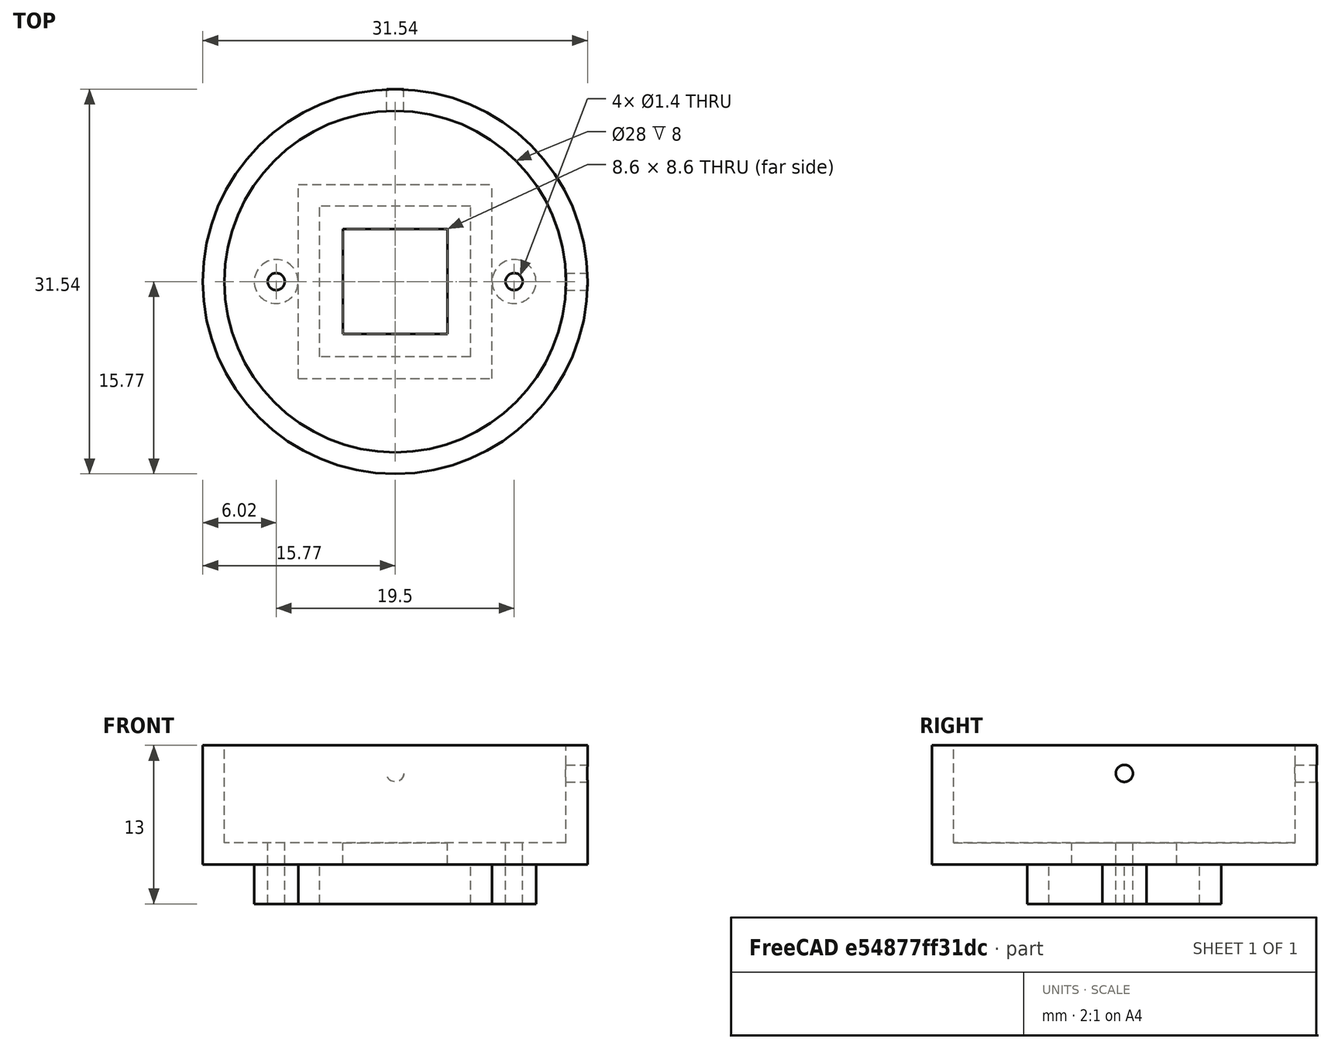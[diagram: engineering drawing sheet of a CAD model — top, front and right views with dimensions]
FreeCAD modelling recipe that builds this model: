
FCSTD DOCUMENT  (FreeCAD 0.16R6706 (Git))
Label: S2H-cam-lens-classic-mounting
License: All rights reserved
LicenseURL: http://en.wikipedia.org/wiki/All_rights_reserved
objects: Part::Cylinder×7, Part::Cut×5, Part::Thickness×4, Part::Box×2, Part::MultiFuse×1
note: 19 computed .brp shape members not serialized (recipe doc carries the construction recipe); baked Part::Feature solids carry a one-line shape summary decoded from their .brp

FEATURE [Part::Cylinder] Cylinder
  Angle = 360
  Height = 8
  Placement = pos=(0,0,5) rot=(0,0,1;0rad)
  Radius = 14
FEATURE [Part::Thickness] Thickness
  Faces = -> Cylinder [Face2]
  Intersection = false
  Join = 2
  Mode = 0
  SelfIntersection = false
  Value = 1.77
FEATURE [Part::Box] Box  label="Cube"
  Height = 3.23
  Length = 15.9
  Placement = pos=(-7.95,-7.95,0) rot=(0,0,1;0rad)
  Width = 15.9
FEATURE [Part::Box] Box001  label="Cube001"
  Height = 1.77
  Length = 8.6
  Placement = pos=(-4.3,-4.3,3.23) rot=(0,0,1;0rad)
  Width = 8.6
FEATURE [Part::Thickness] Thickness001
  Faces = -> Box [Face6,Face5]
  Intersection = false
  Join = 2
  Mode = 0
  SelfIntersection = false
  Value = -1.771
FEATURE [Part::Cut] Cut
  Base = -> Thickness
  Tool = -> Box001
FEATURE [Part::Cylinder] Cylinder001
  Angle = 360
  Height = 3.23
  Radius = 1.8
FEATURE [Part::Thickness] Thickness002
  Faces = -> Cylinder001 [Face2,Face3]
  Intersection = false
  Join = 0
  Mode = 0
  Placement = pos=(9.75,0,0) rot=(0,0,1;0rad)
  SelfIntersection = false
  Value = -1.1
FEATURE [Part::Cylinder] Cylinder002
  Angle = 360
  Height = 10
  Placement = pos=(9.75,0,0) rot=(0,0,1;0rad)
  Radius = 0.7
FEATURE [Part::Cylinder] Cylinder003
  Angle = 360
  Height = 3.23
  Radius = 1.8
FEATURE [Part::Thickness] Thickness003
  Faces = -> Cylinder003 [Face2,Face3]
  Intersection = false
  Join = 0
  Mode = 0
  Placement = pos=(-9.75,0,0) rot=(0,0,1;0rad)
  SelfIntersection = false
  Value = -1.1
FEATURE [Part::Cylinder] Cylinder004
  Angle = 360
  Height = 10
  Placement = pos=(-9.75,0,0) rot=(0,0,1;0rad)
  Radius = 0.7
FEATURE [Part::Cut] Cut001
  Base = -> Cut
  Tool = -> Cylinder002
FEATURE [Part::Cut] Cut002
  Base = -> Cut001
  Tool = -> Cylinder004
FEATURE [Part::Cylinder] Cylinder005
  Angle = 360
  Height = 3
  Placement = pos=(13,0,10.7) rot=(0,1,0;1.5708rad)
  Radius = 0.7
FEATURE [Part::Cylinder] Cylinder006
  Angle = 360
  Height = 3
  Placement = pos=(0,13,10.7) rot=(-1,0,0;1.5708rad)
  Radius = 0.7
FEATURE [Part::Cut] Cut003
  Base = -> Cut002
  Tool = -> Cylinder005
FEATURE [Part::Cut] Cut004
  Base = -> Cut003
  Tool = -> Cylinder006
FEATURE [Part::MultiFuse] Fusion
  Shapes = -> [Thickness001,Thickness002,Thickness003,Cut004]
